FCSTD DOCUMENT  (FreeCAD 0.18R16110 (Git))
Label: 6sideP
License: All rights reserved
LicenseURL: http://en.wikipedia.org/wiki/All_rights_reserved
objects: Sketcher::SketchObject×1
note: 1 computed .brp shape members not serialized (recipe doc carries the construction recipe); baked Part::Feature solids carry a one-line shape summary decoded from their .brp

FEATURE [Sketcher::SketchObject] Sketch
  sketch-geometry (25):
    g0: Circle [constr] CenterX=0 CenterY=0 CenterZ=0 NormalX=0 NormalY=0 NormalZ=1 AngleXU=0 Radius=250
    g1: LineSegment [constr] StartX=-216.506 StartY=125 StartZ=0 EndX=-480.828 EndY=-1.42e-14 EndZ=0
    g2: LineSegment [constr] StartX=-240.414 StartY=416.409 StartZ=0 EndX=0 EndY=250 EndZ=0
    g3: LineSegment [constr] StartX=240.414 StartY=416.409 StartZ=0 EndX=216.506 EndY=125 EndZ=0
    g4: LineSegment [constr] StartX=480.828 StartY=0 StartZ=0 EndX=216.506 EndY=-125 EndZ=0
    g5: LineSegment [constr] StartX=240.414 StartY=-416.409 StartZ=0 EndX=0 EndY=-250 EndZ=0
    g6: LineSegment [constr] StartX=-216.506 StartY=-125 StartZ=0 EndX=-240.414 EndY=-416.409 EndZ=0
    g7: LineSegment [constr] StartX=-30.1066 StartY=248.181 StartZ=0 EndX=-13.1591 EndY=259.108 EndZ=0
    g8: LineSegment [constr] StartX=-13.1591 StartY=259.108 StartZ=0 EndX=-34.3942 EndY=273.807 EndZ=0
    g9: LineSegment [constr] StartX=-34.3942 StartY=273.807 StartZ=0 EndX=-46.1932 EndY=268.532 EndZ=0
    g10: LineSegment [constr] StartX=-46.1932 StartY=268.532 StartZ=0 EndX=-30.1066 EndY=248.181 EndZ=0
    g11: LineSegment StartX=-360.725 StartY=57.833 StartZ=0 EndX=-227.909 EndY=-280.698 EndZ=0
    g12: LineSegment StartX=-227.909 StartY=-280.698 StartZ=0 EndX=130.656 EndY=-341.309 EndZ=0
    g13: LineSegment StartX=130.656 StartY=-341.309 StartZ=0 EndX=360.23 EndY=-59.2834 EndZ=0
    g14: LineSegment StartX=360.23 StartY=-59.2834 StartZ=0 EndX=227.415 EndY=279.247 EndZ=0
    g15: LineSegment StartX=227.415 StartY=279.247 StartZ=0 EndX=-131.15 EndY=339.859 EndZ=0
    g16: LineSegment StartX=-131.15 StartY=339.859 StartZ=0 EndX=-360.725 EndY=57.833 EndZ=0
    g17: LineSegment [constr] StartX=227.415 StartY=279.247 StartZ=0 EndX=130.656 EndY=-341.309 EndZ=0
    g18: LineSegment [constr] StartX=0 StartY=0 StartZ=0 EndX=188.461 EndY=-164.263 EndZ=0
    g19: LineSegment [constr] StartX=0 StartY=0 StartZ=0 EndX=-236.487 EndY=-81.0806 EndZ=0
    g20: LineSegment [constr] StartX=0 StartY=0 StartZ=0 EndX=48.0255 EndY=245.344 EndZ=0
    g21: LineSegment [constr] StartX=-412.383 StartY=-249.515 StartZ=0 EndX=307.504 EndY=-371.203 EndZ=0
    g22: LineSegment [constr] StartX=-307.362 StartY=371.772 StartZ=0 EndX=412.525 EndY=250.083 EndZ=0
    g23: LineSegment [constr] StartX=307.504 StartY=-371.203 StartZ=0 EndX=412.525 EndY=250.083 EndZ=0
    g24: LineSegment [constr] StartX=-307.362 StartY=371.772 StartZ=0 EndX=-412.383 EndY=-249.515 EndZ=0
  constraints (44):
    c: PointOnObject(g1,g-1)
    c: PointOnObject(g5,g0)
    c: PointOnObject(g4,g0)
    c: PointOnObject(g3,g0)
    c: PointOnObject(g2,g0)
    c: Coincident(g0,g-1)
    c: Radius(g0) = 250
    c: PointOnObject(g7,g0)
    c: PointOnObject(g7,g2)
    c: Coincident(g7,g8)
    c: PointOnObject(g8,g2)
    c: Coincident(g8,g9)
    c: Coincident(g9,g10)
    c: Coincident(g10,g7)
    c: Coincident(g11,g12)
    c: Coincident(g12,g13)
    c: Coincident(g13,g14)
    c: Coincident(g14,g15)
    c: Coincident(g15,g16)
    c: Equal(g11, g12-g16) x5
    c: Coincident(g17,g14)
    c: Coincident(g17,g12)
    c: Coincident(g11,g16)
    c: Coincident(g18,g-1)
    c: Coincident(g19,g-1)
    c: Coincident(g20,g-1)
    c: Angle(g19,g18) = 2.0944
    c: Angle(g18,g20) = 2.0944
    c: Equal(g18,g20)
    c: Equal(g20,g19)
    c: Distance(g18) = 250
    c: Coincident(g23,g21)
    c: Coincident(g23,g22)
    c: Coincident(g24,g22)
    c: Coincident(g24,g21)
    c: Perpendicular(g23,g22)
    c: Perpendicular(g23,g21)
    c: Perpendicular(g24,g21)
    c: Parallel(g15,g22)
    c: Parallel(g21,g12)
    c: Distance(g24) = 630.1
    c: Distance(g21) = 730.1
    c: PointOnObject(g13,g23)
    c: PointOnObject(g12,g21)
